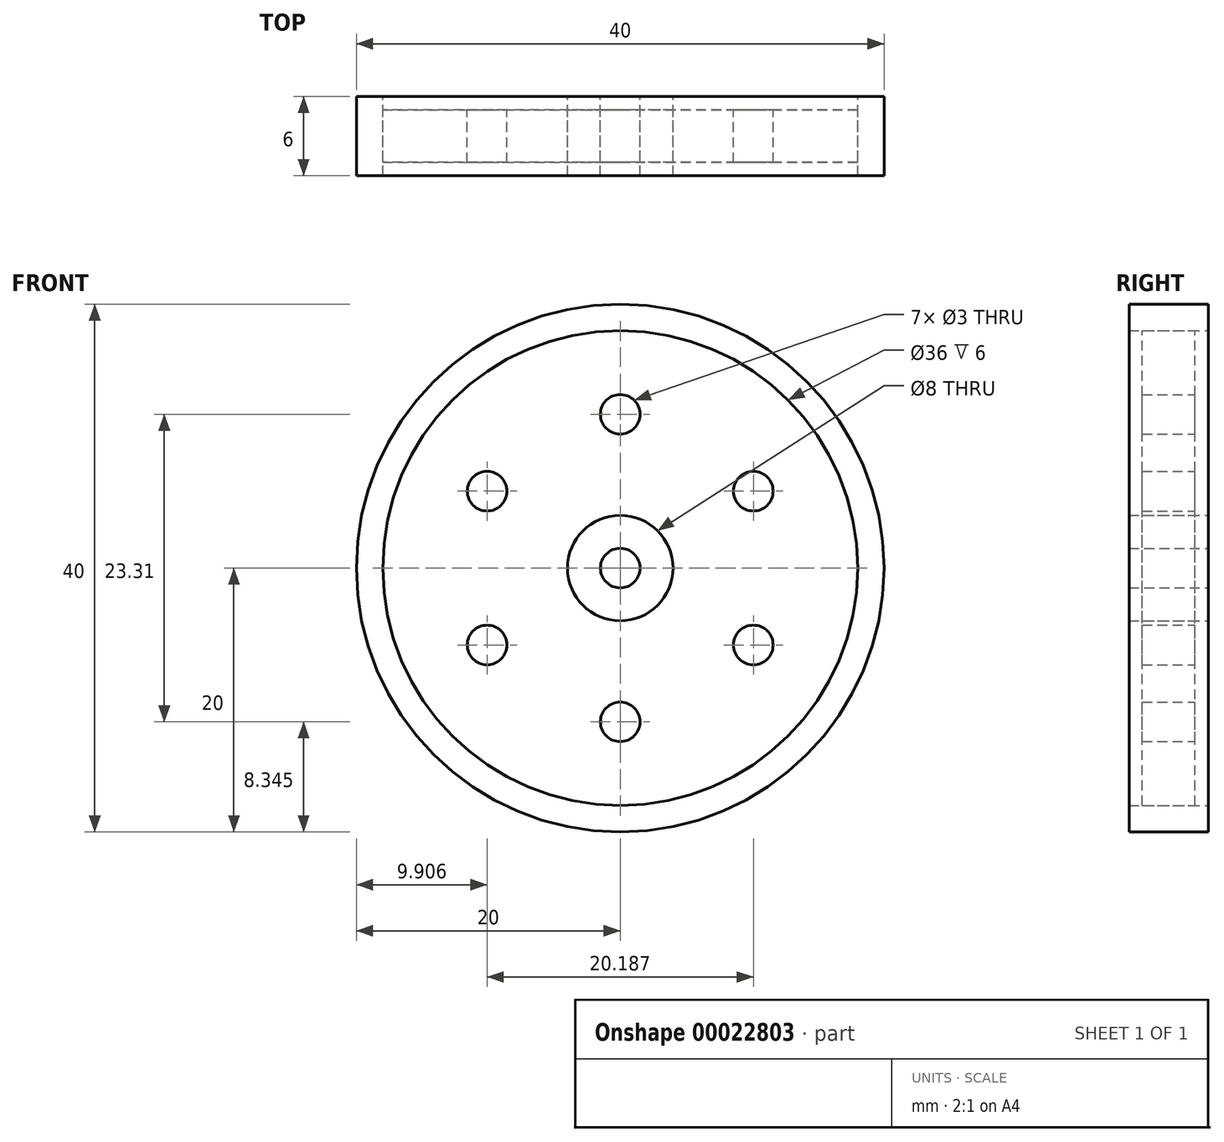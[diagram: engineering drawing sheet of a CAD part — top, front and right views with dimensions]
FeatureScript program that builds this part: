
annotation { "Feature Type Name" : "Feature", "Feature Type Description" : "" }
export const myFeature = defineFeature(function(context is Context, id is Id, definition is map)
    precondition{}
    {
        {
            var Q0;
            Q0=qCreatedBy(makeId("Front.planeOp"),FACE);
            var sketch = newSketch(context, id + "F0", { "sketchPlane" : qUnion([Q0])});
            skCircle(sketch, "E0", {"center": v(0, 11.66) * mm, "radius": 1.5 * mm});
            skCircle(sketch, "E1.1.0", {"center": v(-10.1, 5.83) * mm, "radius": 1.5 * mm});
            skCircle(sketch, "E1.2.0", {"center": v(-10.1, -5.83) * mm, "radius": 1.5 * mm});
            skCircle(sketch, "E1.3.0", {"center": v(0, -11.66) * mm, "radius": 1.5 * mm});
            skCircle(sketch, "E1.4.0", {"center": v(10.1, -5.83) * mm, "radius": 1.5 * mm});
            skCircle(sketch, "E1.5.0", {"center": v(10.1, 5.83) * mm, "radius": 1.5 * mm});
            skPoint(sketch, "E1.center", {"position": v(0, 0) * mm});
            skCircle(sketch, "E2", {"center": v(0, 0) * mm, "radius": 1.5 * mm});
            skCircle(sketch, "E3", {"center": v(0, 0) * mm, "radius": 4 * mm});
            skCircle(sketch, "E4", {"center": v(0, 0) * mm, "radius": 20 * mm});
            skCircle(sketch, "E5", {"center": v(0, 0) * mm, "radius": 18 * mm});
            skSolve(sketch);
        }
        {
            var Q0;
            Q0=makeQuery(id+"F0.imprint","IMPRINT",FACE,{"disambiguationData":[TD([[makeQuery(id+"F0.imprint","IMPRINT",EDGE,{"derivedFrom":sQuery(id+"F0.wireOp",EDGE,"E2")}),-1.0]])]});
            extrude(context, id + "F1", {"entities" : qUnion([Q0]), "endBound" : BoundingType.SYMMETRIC, "depth" : 6 * mm});
        }
        {
            var Q0;
            Q0=makeQuery(id+"F0.imprint","IMPRINT",FACE,{"disambiguationData":[TD([[makeQuery(id+"F0.imprint","IMPRINT",EDGE,{"derivedFrom":sQuery(id+"F0.wireOp",EDGE,"E4")}),1.0]])]});
            extrude(context, id + "F2", {"entities" : qUnion([Q0]), "endBound" : BoundingType.SYMMETRIC, "depth" : 6 * mm});
        }
        {
            var Q0;
            Q0=makeQuery(id+"F0.imprint","IMPRINT",FACE,{"disambiguationData":[TD([[makeQuery(id+"F0.imprint","IMPRINT",EDGE,{"derivedFrom":sQuery(id+"F0.wireOp",EDGE,"E0")}),-1.0]])]});
            extrude(context, id + "F3", {"entities" : qUnion([Q0]), "endBound" : BoundingType.SYMMETRIC, "depth" : 4 * mm});
        }
    });
